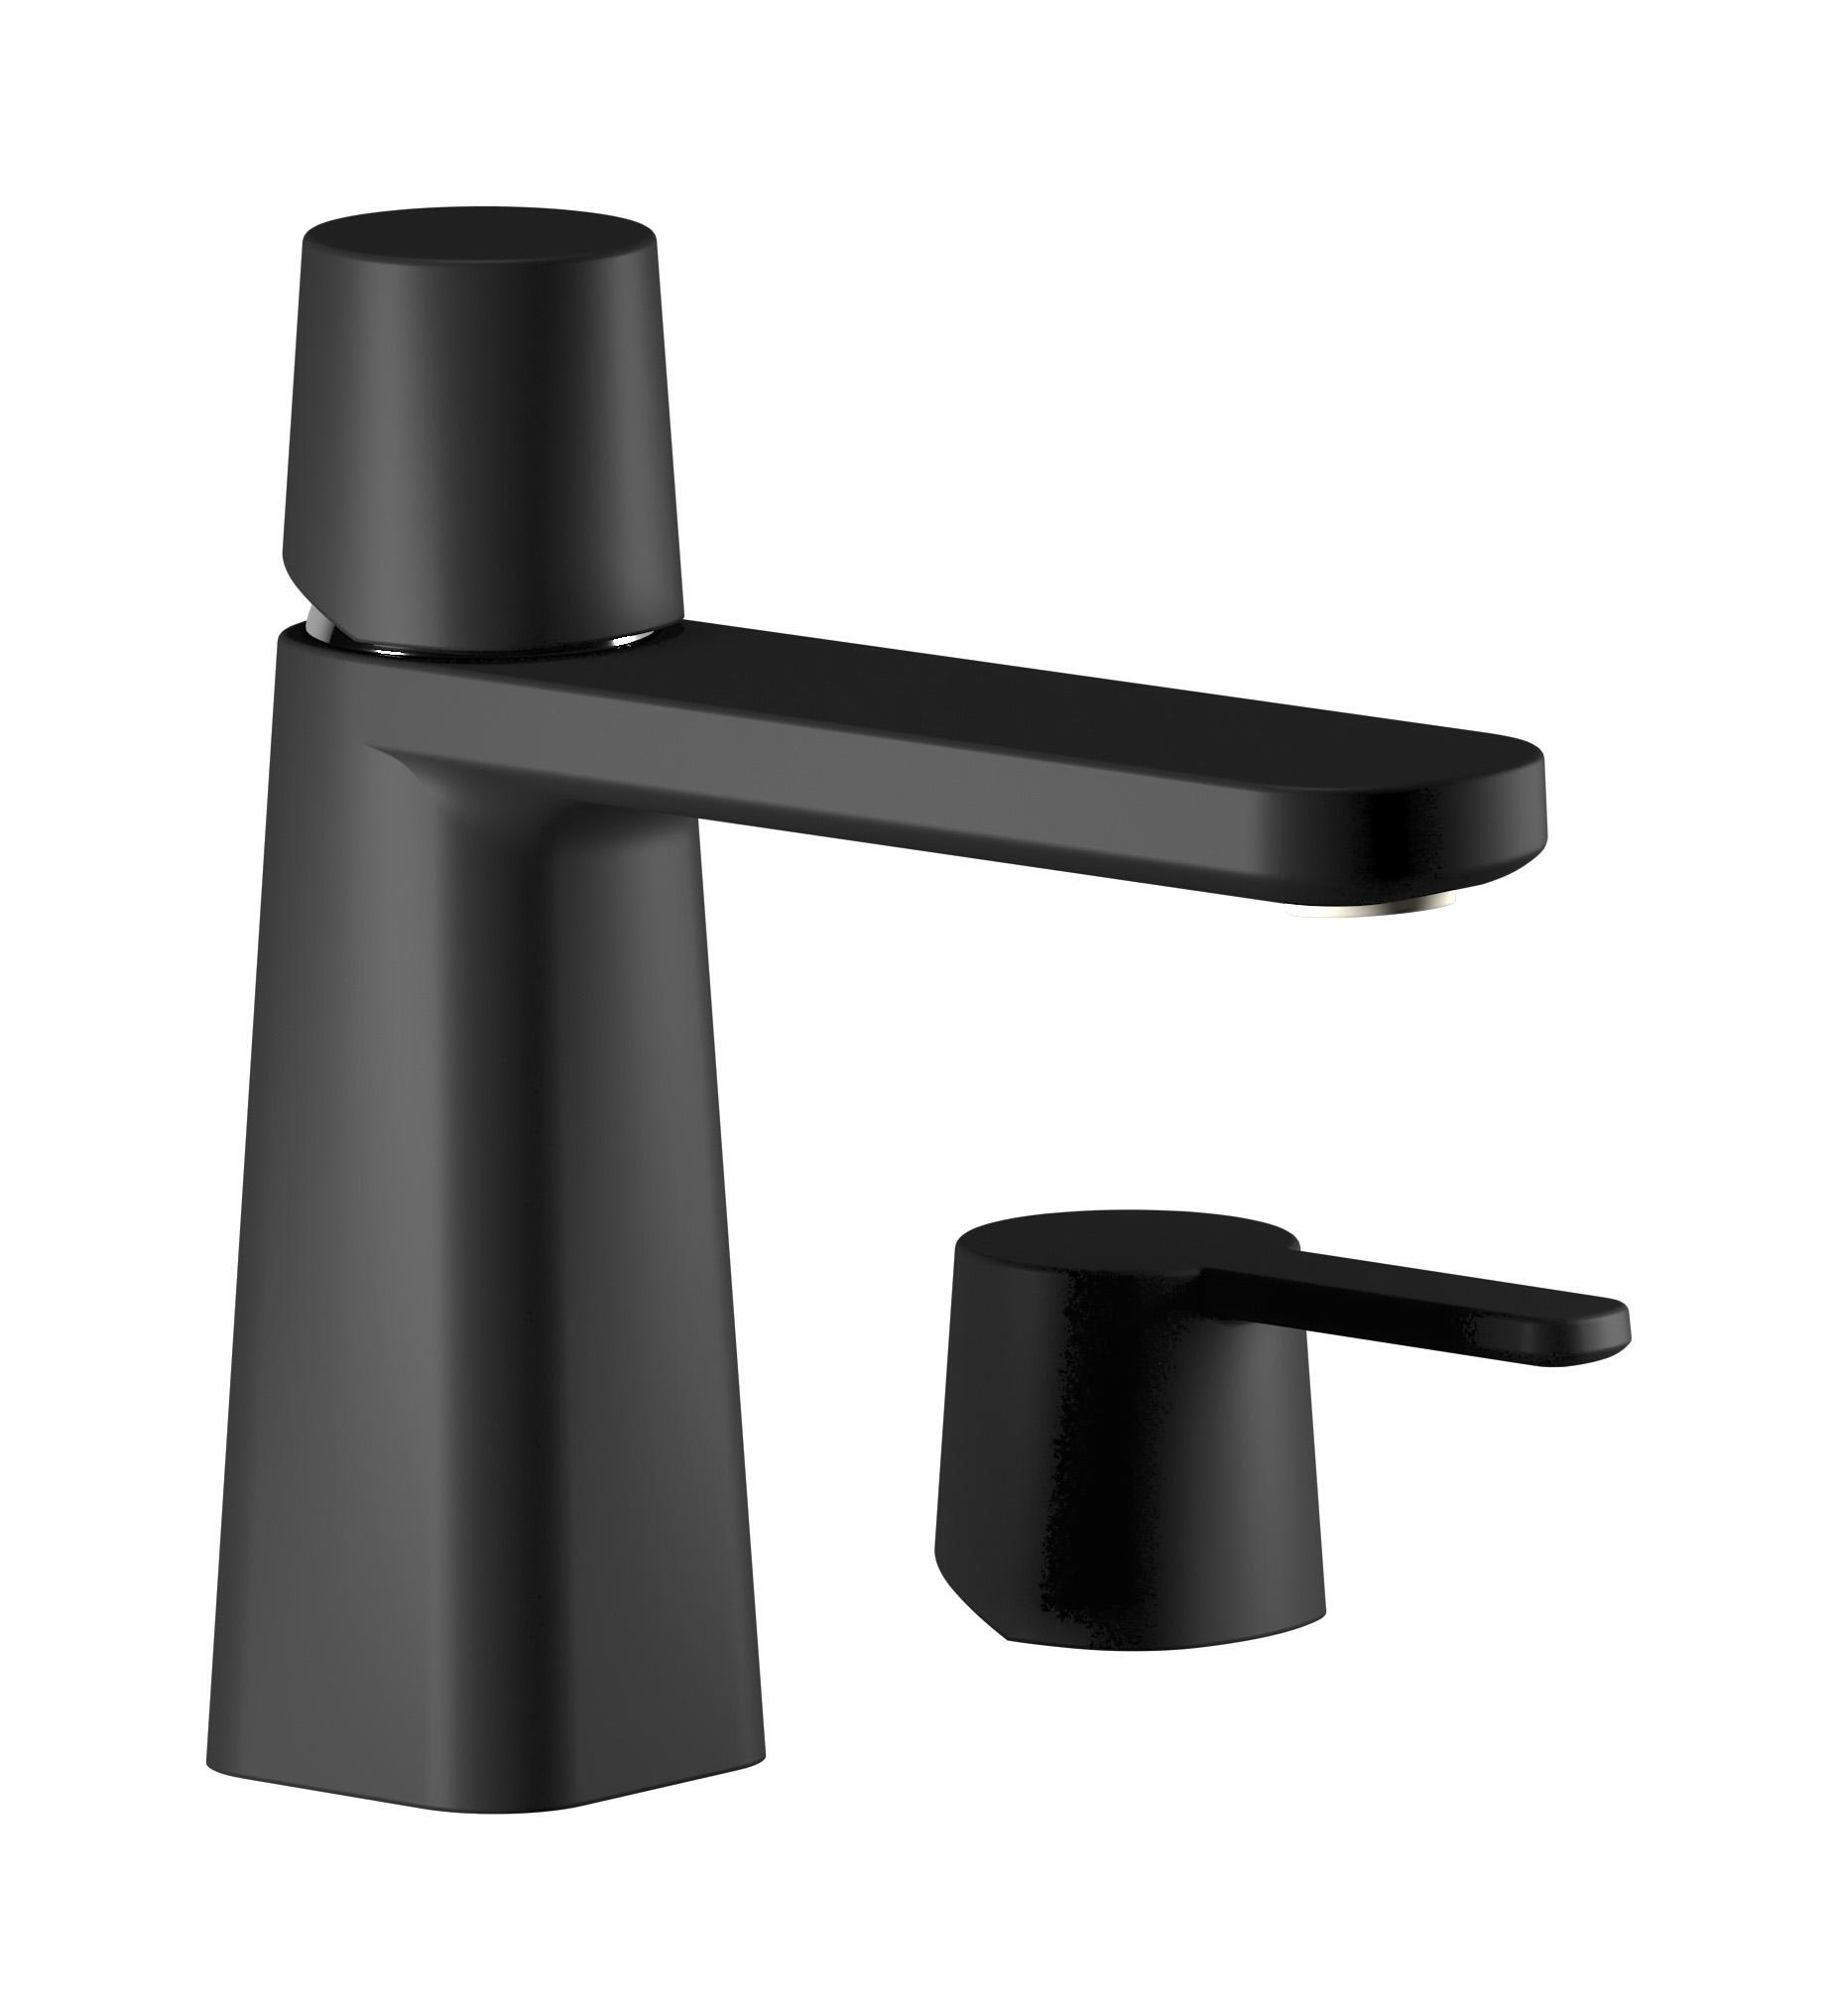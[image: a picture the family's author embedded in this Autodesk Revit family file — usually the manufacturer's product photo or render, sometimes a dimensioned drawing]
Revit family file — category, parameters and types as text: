
# Revit family: AA200
name_source: partatom
category: Apparecchi idraulici
units: mm (PartAtom-declared; Revit-internal decimal feet)

## family parameters
Basato su piano di lavoro = No
Condiviso = No
Mantieni orientamento annotazione = No
Numero OmniClass = 23.45.55.17
Punto di calcolo locali = No
Quota connettore circolare = Usa diametro
Sempre verticale = Sì
Taglio con vuoti quando caricato = No
Tipo di parte = Normale
Titolo OmniClass = Mixing Faucets

## types (5) — shared parameters
Cold water inlet = 10 mm  [stored 0.0328084 ft]
Commenti sul tipo = Washbasin mixer
Connessione CW = No
Connessione HW = No
Connessione di scarico = No
Connessione di ventilazione = No
Descrizione = Monohole washbasin mixer complete with drain
Hot water inlet = 10 mm  [stored 0.0328084 ft]
Produttore = IB Rubinetterie S.p.A.
URL = https://www.weareib.it
zero-valued in all types: Prospetto di default

## per-type parameters (varying)
| type | Finishes surface | Immagine tipo | Modello |
| Chrome | IB_Chrome | AA200CC.jpg | AA200CC |
| Brushed nickel | IB_Brushed nickel | AA200SS.jpg | AA200SS |
| Matt black | IB_matt black | AA200NP.jpg | AA200NP |
| Matt white | IB_matt white | AA200BO.jpg | AA200BO |
| Brushed gold | IB_brushed gold | AA200OS.jpg | AA200OS |

note: [stored X ft] marks values corroborated as IEEE doubles in the binary element streams (Revit-internal decimal feet)
